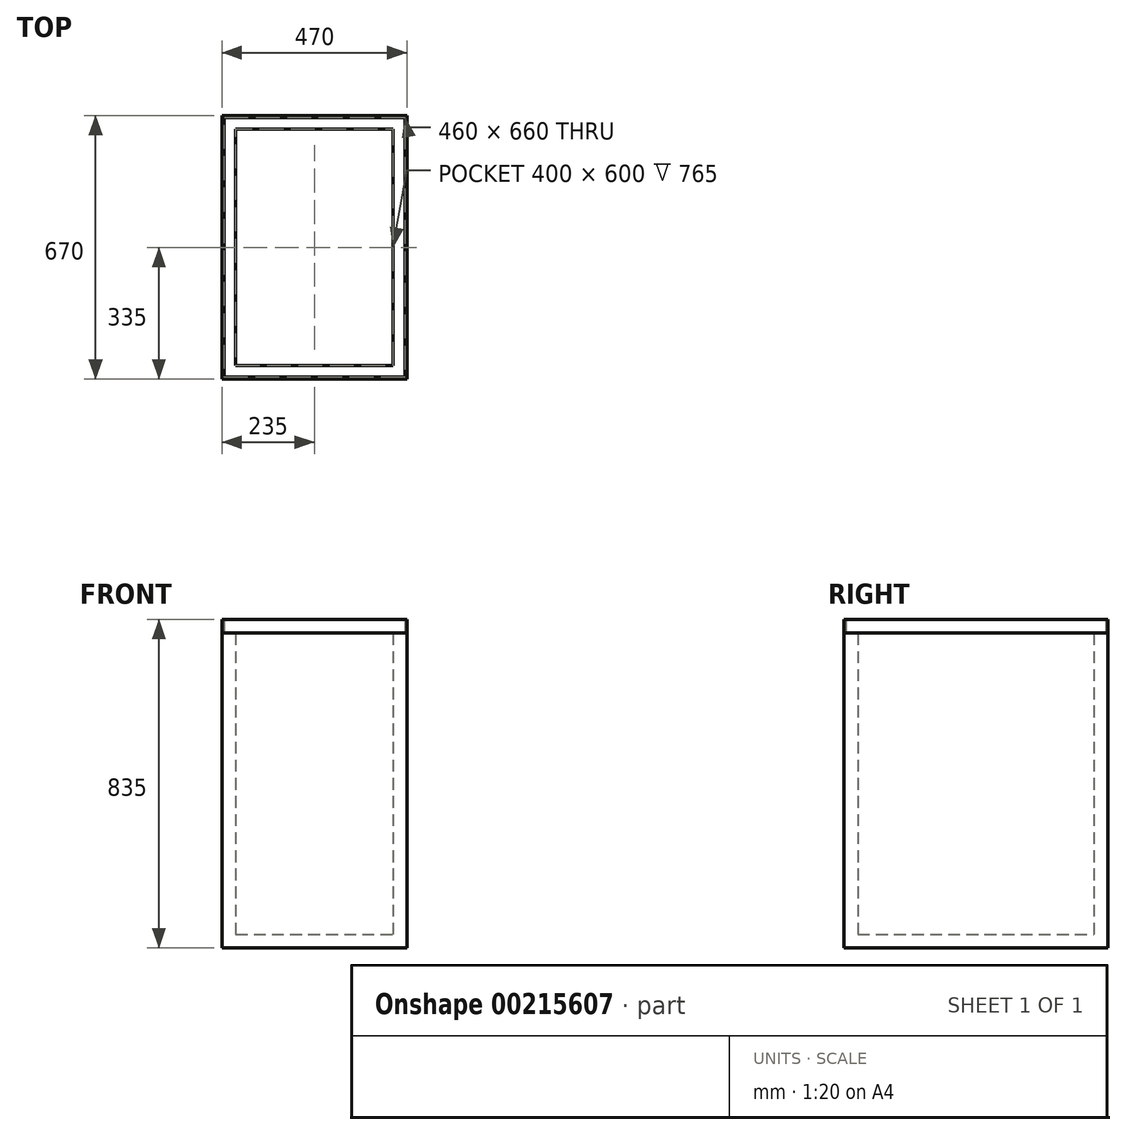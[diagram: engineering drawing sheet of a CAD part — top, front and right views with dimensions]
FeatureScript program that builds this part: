
annotation { "Feature Type Name" : "Feature", "Feature Type Description" : "" }
export const myFeature = defineFeature(function(context is Context, id is Id, definition is map)
    precondition{}
    {
        {
            var Q0;
            Q0=qCreatedBy(makeId("Top.planeOp"),FACE);
            var sketch = newSketch(context, id + "F0", { "sketchPlane" : qUnion([Q0])});
            skPoint(sketch, "E0.middle", {"position": v(0, 0) * mm});
            skLineSegment(sketch, "E1.0", {"start": v(-235, -335) * mm, "end": v(-235, 335) * mm});
            skLineSegment(sketch, "E1.1", {"start": v(-235, -335) * mm, "end": v(235, -335) * mm});
            skLineSegment(sketch, "E1.2", {"start": v(235, -335) * mm, "end": v(235, 335) * mm});
            skLineSegment(sketch, "E1.3", {"start": v(-235, 335) * mm, "end": v(235, 335) * mm});
            skPoint(sketch, "E0.top.start.orphan", {"position": v(-200, 300) * mm});
            skPoint(sketch, "E0.right.end.orphan", {"position": v(200, 300) * mm});
            skPoint(sketch, "E0.bottom.end.orphan", {"position": v(200, -300) * mm});
            skPoint(sketch, "E0.bottom.start.orphan", {"position": v(-200, -300) * mm});
            skSolve(sketch);
        }
        {
            var Q0;
            Q0 = qSketchRegion(id + "F0", true);
            extrude(context, id + "F1", {"entities" : qUnion([Q0]), "depth" : 800 * mm});
        }
        {
            var Q0;
            Q0=makeQuery(id+"F1.opExtrude","CAP_FACE",FACE,{"disambiguationData":[OSD([sQuery(id+"F0.wireOp",EDGE,"E1.0"),sQuery(id+"F0.wireOp",EDGE,"E1.1"),sQuery(id+"F0.wireOp",EDGE,"E1.2"),sQuery(id+"F0.wireOp",EDGE,"E1.3")])],"isStart":false});
            shell(context, id + "F2", {"entities" : qUnion([Q0]), "thickness" : 35 * mm});
        }
        {
            var Q0;
            Q0=makeQuery(id+"F1.opExtrude","CAP_FACE",FACE,{"disambiguationData":[OSD([sQuery(id+"F0.wireOp",EDGE,"E1.0"),sQuery(id+"F0.wireOp",EDGE,"E1.1"),sQuery(id+"F0.wireOp",EDGE,"E1.2"),sQuery(id+"F0.wireOp",EDGE,"E1.3")])],"isStart":false});
            var sketch = newSketch(context, id + "F3", { "sketchPlane" : qUnion([Q0])});
            skLineSegment(sketch, "E2.0", {"start": v(-230, -330) * mm, "end": v(-230, 330) * mm});
            skLineSegment(sketch, "E2.1", {"start": v(-230, -330) * mm, "end": v(230, -330) * mm});
            skLineSegment(sketch, "E2.2", {"start": v(230, -330) * mm, "end": v(230, 330) * mm});
            skLineSegment(sketch, "E2.3", {"start": v(-230, 330) * mm, "end": v(230, 330) * mm});
            skSolve(sketch);
        }
        {
            var Q0;
            Q0=makeQuery(id+"F3.imprint","IMPRINT",FACE,{"disambiguationData":[TD([[makeQuery(id+"F3.imprint","IMPRINT",EDGE,{"derivedFrom":sQuery(id+"F3.wireOp",EDGE,"E2.0")}),1.0]])]});
            extrude(context, id + "F4", {"entities" : qUnion([Q0]), "depth" : 35 * mm});
        }
    });
